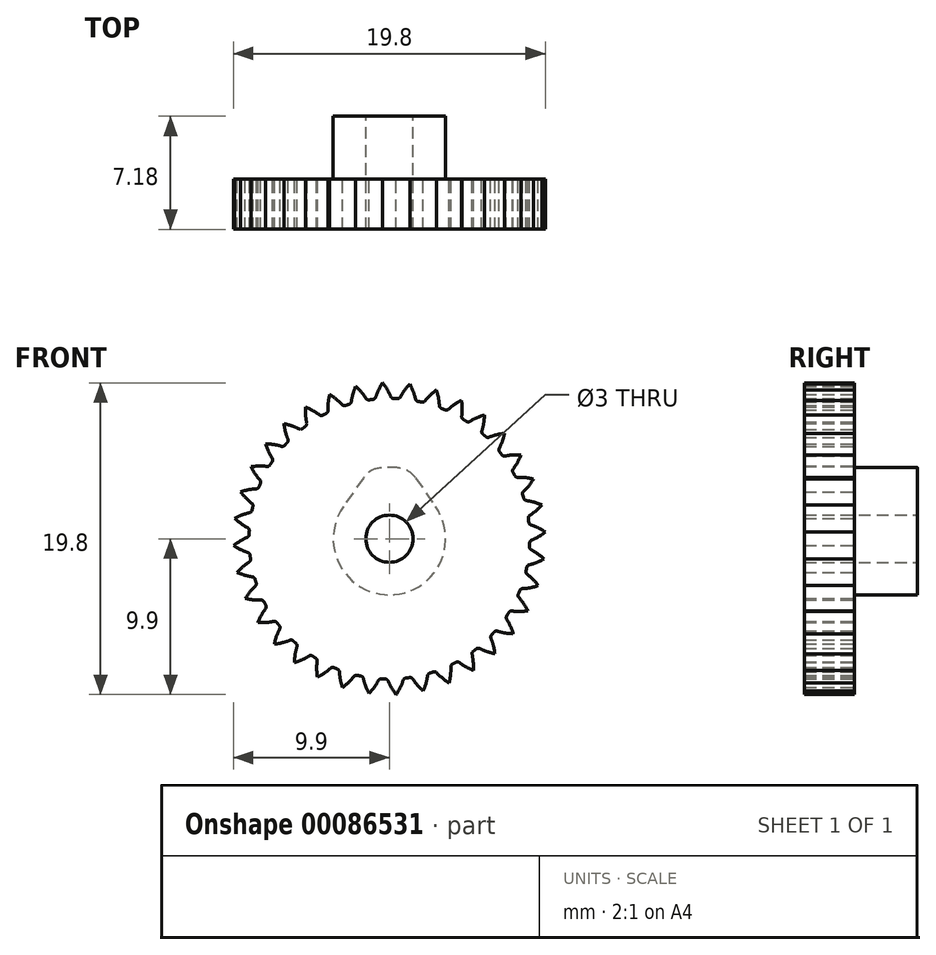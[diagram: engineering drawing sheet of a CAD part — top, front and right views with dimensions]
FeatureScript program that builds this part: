
annotation { "Feature Type Name" : "Feature", "Feature Type Description" : "" }
export const myFeature = defineFeature(function(context is Context, id is Id, definition is map)
    precondition{}
    {
        {
            assignVariable(context, id + "F0", {"name" : "Teeth", "anyValue" : 36});
        }
        {
            var Q0;
            Q0=qCreatedBy(makeId("Front.planeOp"),FACE);
            var sketch = newSketch(context, id + "F1", { "sketchPlane" : qUnion([Q0])});
            skCircle(sketch, "E0", {"center": v(0, 0) * mm, "radius": 8.49 * mm, "construction": true});
            skLineSegment(sketch, "E1", {"start": v(0, 0) * mm, "end": v(-0.32, 8.48) * mm, "construction": true});
            skLineSegment(sketch, "E2", {"start": v(0, 0) * mm, "end": v(-0.87, 8.44) * mm, "construction": true});
            skLineSegment(sketch, "E3", {"start": v(0, 0) * mm, "end": v(-1.41, 8.37) * mm, "construction": true});
            skLineSegment(sketch, "E4", {"start": v(-1.41, 8.37) * mm, "end": v(0.2, 8.64) * mm, "construction": true});
            skLineSegment(sketch, "E5", {"start": v(0, 0) * mm, "end": v(-1.95, 8.26) * mm, "construction": true});
            skLineSegment(sketch, "E6", {"start": v(-1.95, 8.26) * mm, "end": v(0.18, 8.76) * mm, "construction": true});
            skLineSegment(sketch, "E7", {"start": v(-1.41, 8.37) * mm, "end": v(-0.87, 8.44) * mm, "construction": true});
            skLineSegment(sketch, "E8", {"start": v(-1.95, 8.26) * mm, "end": v(-1.41, 8.37) * mm, "construction": true});
            skLineSegment(sketch, "E9", {"start": v(-1.41, 8.37) * mm, "end": v(-0.32, 8.48) * mm, "construction": true});
            skLineSegment(sketch, "E10", {"start": v(-1.95, 8.26) * mm, "end": v(-0.32, 8.48) * mm, "construction": true});
            skLineSegment(sketch, "E11", {"start": v(0, 0) * mm, "end": v(-3.5, 7.73) * mm, "construction": true});
            skLineSegment(sketch, "E12", {"start": v(-3.5, 7.73) * mm, "end": v(-0.04, 9.3) * mm, "construction": true});
            skLineSegment(sketch, "E13", {"start": v(0, 0) * mm, "end": v(-3, 7.94) * mm, "construction": true});
            skLineSegment(sketch, "E14", {"start": v(-3, 7.94) * mm, "end": v(0.06, 9.1) * mm, "construction": true});
            skLineSegment(sketch, "E15", {"start": v(0, 0) * mm, "end": v(-2.48, 8.12) * mm, "construction": true});
            skLineSegment(sketch, "E16", {"start": v(-2.48, 8.12) * mm, "end": v(0.13, 8.91) * mm, "construction": true});
            skLineSegment(sketch, "E17", {"start": v(-2.48, 8.12) * mm, "end": v(-1.95, 8.26) * mm, "construction": true});
            skLineSegment(sketch, "E18", {"start": v(-2.48, 8.12) * mm, "end": v(-3, 7.94) * mm, "construction": true});
            skLineSegment(sketch, "E19", {"start": v(-3, 7.94) * mm, "end": v(-3.5, 7.73) * mm, "construction": true});
            skLineSegment(sketch, "E20", {"start": v(-2.48, 8.12) * mm, "end": v(-0.32, 8.48) * mm, "construction": true});
            skLineSegment(sketch, "E21", {"start": v(-3, 7.94) * mm, "end": v(-0.32, 8.48) * mm, "construction": true});
            skLineSegment(sketch, "E22", {"start": v(-3.5, 7.73) * mm, "end": v(-0.32, 8.48) * mm, "construction": true});
            skLineSegment(sketch, "E23", {"start": v(0, 0) * mm, "end": v(-4.47, 7.21) * mm, "construction": true});
            skLineSegment(sketch, "E24", {"start": v(-4.47, 7.21) * mm, "end": v(-0.34, 9.78) * mm, "construction": true});
            skLineSegment(sketch, "E25", {"start": v(0, 0) * mm, "end": v(-4.93, 6.9) * mm, "construction": true});
            skLineSegment(sketch, "E26", {"start": v(-4.93, 6.9) * mm, "end": v(-0.54, 10.04) * mm, "construction": true});
            skLineSegment(sketch, "E27", {"start": v(0, 0) * mm, "end": v(-5.37, 6.58) * mm, "construction": true});
            skLineSegment(sketch, "E28", {"start": v(0, 0) * mm, "end": v(-4, 7.49) * mm, "construction": true});
            skLineSegment(sketch, "E29", {"start": v(-4, 7.49) * mm, "end": v(-0.17, 9.53) * mm, "construction": true});
            skLineSegment(sketch, "E30", {"start": v(-3.5, 7.73) * mm, "end": v(-4, 7.49) * mm, "construction": true});
            skLineSegment(sketch, "E31", {"start": v(-4, 7.49) * mm, "end": v(-4.47, 7.21) * mm, "construction": true});
            skLineSegment(sketch, "E32", {"start": v(-4.47, 7.21) * mm, "end": v(-4.93, 6.9) * mm, "construction": true});
            skLineSegment(sketch, "E33", {"start": v(-4.93, 6.9) * mm, "end": v(-5.37, 6.58) * mm, "construction": true});
            skLineSegment(sketch, "E34", {"start": v(-0.32, 8.48) * mm, "end": v(-4, 7.49) * mm, "construction": true});
            skLineSegment(sketch, "E35", {"start": v(-0.32, 8.48) * mm, "end": v(-4.47, 7.21) * mm, "construction": true});
            skLineSegment(sketch, "E36", {"start": v(-0.32, 8.48) * mm, "end": v(-4.93, 6.9) * mm, "construction": true});
            skLineSegment(sketch, "E37", {"start": v(-0.32, 8.48) * mm, "end": v(-5.37, 6.58) * mm, "construction": true});
            skCircle(sketch, "E38", {"center": v(0, 0) * mm, "radius": 9.53 * mm, "construction": true});
            skCircle(sketch, "E39", {"center": v(0, 0) * mm, "radius": 10.05 * mm});
            skPoint(sketch, "E40", {"position": v(0, 9.53) * mm});
            skLineSegment(sketch, "E41", {"start": v(0, 0) * mm, "end": v(-0.38, 8.6) * mm, "construction": true});
            skPoint(sketch, "E42.MirrorP", {"position": v(-0.83, 9.49) * mm});
            skLineSegment(sketch, "E43", {"start": v(-0.83, 9.49) * mm, "end": v(0, 0) * mm, "construction": true});
            skLineSegment(sketch, "E44", {"start": v(0, 0) * mm, "end": v(0, 9.53) * mm, "construction": true});
            skLineSegment(sketch, "E45", {"start": v(-0.87, 8.44) * mm, "end": v(-0.32, 8.48) * mm, "construction": true});
            skLineSegment(sketch, "E46", {"start": v(0.2, 8.64) * mm, "end": v(0.18, 8.76) * mm, "construction": true});
            skLineSegment(sketch, "E47", {"start": v(0, 0) * mm, "end": v(0, 10.19) * mm, "construction": true});
            skCircle(sketch, "E48", {"center": v(0, 0) * mm, "radius": 8.91 * mm});
            skSolve(sketch);
        }
        {
            var Q0;
            Q0=qCreatedBy(makeId("Front.planeOp"),FACE);
            var sketch = newSketch(context, id + "F2", { "sketchPlane" : qUnion([Q0])});
            skCircle(sketch, "E49.0", {"center": v(0, 0) * mm, "radius": 9.53 * mm, "construction": true});
            skPoint(sketch, "E50.0", {"position": v(-0.54, 10.04) * mm});
            skPoint(sketch, "E50.1", {"position": v(-0.34, 9.78) * mm});
            skPoint(sketch, "E50.2", {"position": v(-0.17, 9.53) * mm});
            skPoint(sketch, "E50.3", {"position": v(-0.04, 9.3) * mm});
            skPoint(sketch, "E50.4", {"position": v(0.06, 9.1) * mm});
            skPoint(sketch, "E50.6", {"position": v(0.18, 8.76) * mm});
            skPoint(sketch, "E50.7", {"position": v(0.2, 8.64) * mm});
            skPoint(sketch, "E50.8", {"position": v(0.13, 8.91) * mm});
            skLineSegment(sketch, "E51.0", {"start": v(0, 0) * mm, "end": v(-0.38, 8.6) * mm, "construction": true});
            skFitSpline(sketch, "E52", {"points": [v(-0.54, 10.04) * mm, v(-0.34, 9.78) * mm, v(-0.17, 9.53) * mm, v(-0.04, 9.3) * mm, v(0.06, 9.1) * mm, v(0.13, 8.91) * mm, v(0.18, 8.76) * mm, v(0.2, 8.64) * mm], "startDerivative": vector(3.53, -4.5) * mm, "endDerivative": vector(0.8, -3.4) * mm});
            skFitSpline(sketch, "E53.MirrorCS", {"points": [v(-0.34, 10.05) * mm, v(-0.52, 9.77) * mm, v(-0.66, 9.5) * mm, v(-0.77, 9.27) * mm, v(-0.85, 9.06) * mm, v(-0.9, 8.87) * mm, v(-0.94, 8.71) * mm, v(-0.96, 8.6) * mm], "startDerivative": vector(-3.13, -4.8) * mm, "endDerivative": vector(-0.5, -3.46) * mm});
            skCircle(sketch, "E54", {"center": v(0, 0) * mm, "radius": 1.5 * mm});
            skCircle(sketch, "E55.0", {"center": v(0, 0) * mm, "radius": 8.91 * mm});
            skArc(sketch, "E56", {"start": v(-0.54, 10.04) * mm, "mid": v(0.44, -10.04) * mm, "end": v(-0.34, 10.05) * mm});
            skLineSegment(sketch, "E57", {"start": v(-0.96, 8.6) * mm, "end": v(0, 0) * mm});
            skLineSegment(sketch, "E58", {"start": v(0, 0) * mm, "end": v(0.2, 8.64) * mm});
            skSolve(sketch);
        }
        {
            var Q0;
            {var subQ1=sQuery(id+"F2.wireOp",EDGE,"E52");var subQ9=sQuery(id+"F2.wireOp",EDGE,"rA0usyOi-Jm6w-jZNR-JSDv-ujEcH4bsm2Ol");var subQ11=makeQuery(id+"F2.imprint","INTERSECT",VERTEX,{"derivedFrom":[subQ1,subQ9]});Q0=makeQuery(id+"F2.imprint","IMPRINT",FACE,{"disambiguationData":[TD([[makeQuery(id+"F2.imprint","IMPRINT",EDGE,{"disambiguationData":[TD([[subQ11,1.0]])],"derivedFrom":subQ1}),-1.0]])]});}
            var Q1;
            {var subQ0=sQuery(id+"F2.wireOp",EDGE,"QqPcIgQ4-TZE6-73E5-WQaq-ugCT5JtziKyn");var subQ1=sQuery(id+"F2.wireOp",EDGE,"90be38e0-c88f-493d-85a8-1201295b9109.0");var subQ2=makeQuery(id+"F2.imprint","INTERSECT",VERTEX,{"derivedFrom":[subQ1,subQ0]});Q1=makeQuery(id+"F2.imprint","IMPRINT",FACE,{"disambiguationData":[TD([[makeQuery(id+"F2.imprint","IMPRINT",EDGE,{"disambiguationData":[TD([[subQ2,1.0]])],"derivedFrom":subQ1}),1.0]])]});}
            var Q2;
            {var subQ0=sQuery(id+"F2.wireOp",EDGE,"QqPcIgQ4-TZE6-73E5-WQaq-ugCT5JtziKyn");var subQ1=sQuery(id+"F2.wireOp",EDGE,"90be38e0-c88f-493d-85a8-1201295b9109.0");var subQ2=makeQuery(id+"F2.imprint","INTERSECT",VERTEX,{"derivedFrom":[subQ1,subQ0]});Q2=makeQuery(id+"F2.imprint","IMPRINT",FACE,{"disambiguationData":[TD([[makeQuery(id+"F2.imprint","IMPRINT",EDGE,{"disambiguationData":[TD([[subQ2,-1.0]])],"derivedFrom":subQ1}),1.0]])]});}
            var Q3;
            {var subQ1=sQuery(id+"F2.wireOp",EDGE,"E52");var subQ8=sQuery(id+"F2.wireOp",EDGE,"b861a5ab-cd51-40f1-92ab-cea0f5fe0d4d.1");var subQ11=makeQuery(id+"F2.imprint","INTERSECT",VERTEX,{"derivedFrom":[subQ1,subQ8]});Q3=makeQuery(id+"F2.imprint","IMPRINT",FACE,{"disambiguationData":[TD([[makeQuery(id+"F2.imprint","IMPRINT",EDGE,{"disambiguationData":[TD([[subQ11,1.0]])],"derivedFrom":subQ1}),-1.0]])]});}
            var Q4;
            {var subQ0=sQuery(id+"F2.wireOp",EDGE,"b861a5ab-cd51-40f1-92ab-cea0f5fe0d4d.0");var subQ1=sQuery(id+"F2.wireOp",EDGE,"E54");var subQ2=makeQuery(id+"F2.imprint","INTERSECT",VERTEX,{"derivedFrom":[subQ1,subQ0]});Q4=makeQuery(id+"F2.imprint","IMPRINT",FACE,{"disambiguationData":[TD([[makeQuery(id+"F2.imprint","IMPRINT",EDGE,{"disambiguationData":[TD([[subQ2,-1.0]])],"derivedFrom":subQ1}),-1.0]])]});}
            var Q5;
            {var subQ0=sQuery(id+"F2.wireOp",EDGE,"b861a5ab-cd51-40f1-92ab-cea0f5fe0d4d.0");var subQ1=sQuery(id+"F2.wireOp",EDGE,"E54");var subQ2=makeQuery(id+"F2.imprint","INTERSECT",VERTEX,{"derivedFrom":[subQ1,subQ0]});Q5=makeQuery(id+"F2.imprint","IMPRINT",FACE,{"disambiguationData":[TD([[makeQuery(id+"F2.imprint","IMPRINT",EDGE,{"disambiguationData":[TD([[subQ2,1.0]])],"derivedFrom":subQ1}),-1.0]])]});}
            extrude(context, id + "F3", {"entities" : qUnion([Q0, Q1, Q2, Q3, Q4, Q5]), "depth" : 3.17 * mm});
        }
        {
            var Q0;
            Q0=makeQuery(id+"F3.opExtrude","SWEPT_EDGE",EDGE,{"disambiguationData":[OSD([sQuery(id+"F2.wireOp",EDGE,"b861a5ab-cd51-40f1-92ab-cea0f5fe0d4d.1"),sQuery(id+"F2.wireOp",EDGE,"E55.0")])]});
            var Q1;
            Q1=makeQuery(id+"F3.opExtrude","SWEPT_EDGE",EDGE,{"disambiguationData":[OSD([sQuery(id+"F2.wireOp",EDGE,"b861a5ab-cd51-40f1-92ab-cea0f5fe0d4d.0"),sQuery(id+"F2.wireOp",EDGE,"E55.0")])]});
            fillet(context, id + "F4", {"entities" : qUnion([Q0, Q1]), "radius" : 0.2 * mm, "tangentPropagation" : true, "allowEdgeOverflow" : false});
        }
        {
            var Q0;
            Q0=makeQuery(id+"F4.opFillet","BLEND_FACE",FACE,{"disambiguationData":[OSD([sQuery(id+"F2.wireOp",EDGE,"E55.0"),sQuery(id+"F2.wireOp",EDGE,"E57")])]});
            var Q1;
            Q1=makeQuery(id+"F3.opExtrude","SWEPT_FACE",FACE,{"disambiguationData":[OSD([sQuery(id+"F2.wireOp",EDGE,"E57")])]});
            var Q2;
            Q2=makeQuery(id+"F3.opExtrude","SWEPT_FACE",FACE,{"disambiguationData":[OSD([sQuery(id+"F2.wireOp",EDGE,"E53.MirrorCS")])]});
            var Q3;
            Q3=makeQuery(id+"F3.opExtrude","SWEPT_FACE",FACE,{"disambiguationData":[OSD([sQuery(id+"F2.wireOp",EDGE,"E56")])]});
            var Q4;
            Q4=makeQuery(id+"F3.opExtrude","SWEPT_FACE",FACE,{"disambiguationData":[OSD([sQuery(id+"F2.wireOp",EDGE,"E52")])]});
            var Q5;
            Q5=makeQuery(id+"F3.opExtrude","SWEPT_FACE",FACE,{"disambiguationData":[OSD([sQuery(id+"F2.wireOp",EDGE,"E58")])]});
            var Q6;
            Q6=makeQuery(id+"F4.opFillet","BLEND_FACE",FACE,{"disambiguationData":[OSD([sQuery(id+"F2.wireOp",EDGE,"E55.0"),sQuery(id+"F2.wireOp",EDGE,"E58")])]});
            var Q7;
            Q7=makeQuery(id+"F3.opExtrude","SWEPT_FACE",FACE,{"disambiguationData":[OSD([sQuery(id+"F2.wireOp",EDGE,"E55.0")])]});
            circularPattern(context, id + "F5", {"faces" : qUnion([Q0, Q1, Q2, Q3, Q4, Q5, Q6]), "axis" : qUnion([Q7]), "angle" : 360 * degree, "instanceCount" : round(getVariable(context, 'Teeth')), "equalSpace" : true, "patternType" : PatternType.FACE});
        }
        {
            var Q0;
            Q0=makeQuery(id+"F3.opExtrude","CAP_FACE",FACE,{"disambiguationData":[OSD([sQuery(id+"F2.wireOp",EDGE,"E52"),sQuery(id+"F2.wireOp",EDGE,"E53.MirrorCS"),sQuery(id+"F2.wireOp",EDGE,"E54"),sQuery(id+"F2.wireOp",EDGE,"E55.0")])],"isStart":true});
            var sketch = newSketch(context, id + "F6", { "sketchPlane" : qUnion([Q0])});
            skCircle(sketch, "E59", {"center": v(0, 0) * mm, "radius": 3.57 * mm});
            skArc(sketch, "E60", {"start": v(1.33, 4.34) * mm, "mid": v(0, 4.54) * mm, "end": v(-1.33, 4.34) * mm});
            skLineSegment(sketch, "E61", {"start": v(0, 0) * mm, "end": v(0, 6.8) * mm, "construction": true});
            skLineSegment(sketch, "E62", {"start": v(0, 4.54) * mm, "end": v(-1.33, 4.54) * mm, "construction": true});
            skLineSegment(sketch, "E63", {"start": v(0, 4.54) * mm, "end": v(1.33, 4.54) * mm, "construction": true});
            skLineSegment(sketch, "E64", {"start": v(-1.33, 4.54) * mm, "end": v(-1.33, 0) * mm, "construction": true});
            skLineSegment(sketch, "E65", {"start": v(1.33, 4.54) * mm, "end": v(1.33, 0) * mm, "construction": true});
            skPoint(sketch, "E66", {"position": v(-1.33, 4.34) * mm});
            skPoint(sketch, "E67", {"position": v(1.33, 4.34) * mm});
            skLineSegment(sketch, "E68", {"start": v(-1.33, 4.34) * mm, "end": v(-2.93, 2.04) * mm});
            skLineSegment(sketch, "E69", {"start": v(1.33, 4.34) * mm, "end": v(2.93, 2.04) * mm});
            skSolve(sketch);
        }
        {
            var Q0;
            Q0=makeQuery(id+"F6.imprint","IMPRINT",FACE,{"disambiguationData":[TD([[makeQuery(id+"F6.imprint","IMPRINT",EDGE,{"derivedFrom":makeQuery(id+"F3.opExtrude","CAP_EDGE",EDGE,{"disambiguationData":[OSD([sQuery(id+"F2.wireOp",EDGE,"E54")])],"isStart":true})}),1.0]])]});
            var Q1;
            Q1=makeQuery(id+"F6.imprint","IMPRINT",FACE,{"disambiguationData":[TD([[makeQuery(id+"F6.imprint","IMPRINT",EDGE,{"derivedFrom":sQuery(id+"F6.wireOp",EDGE,"E60")}),1.0]])]});
            extrude(context, id + "F7", {"entities" : qUnion([Q0, Q1]), "operationType" : NewBodyOperationType.ADD, "depth" : 4 * mm});
        }
        {
            var Q0;
            Q0=makeQuery(id+"F6.imprint","IMPRINT",FACE,{"disambiguationData":[TD([[makeQuery(id+"F6.imprint","IMPRINT",EDGE,{"derivedFrom":makeQuery(id+"F3.opExtrude","CAP_EDGE",EDGE,{"disambiguationData":[OSD([sQuery(id+"F2.wireOp",EDGE,"E54")])],"isStart":true})}),-1.0]])]});
            extrude(context, id + "F8", {"entities" : qUnion([Q0]), "operationType" : NewBodyOperationType.REMOVE, "depth" : 25 * mm, "symmetric" : true});
        }
        {
            var Q0;
            Q0=makeQuery(id+"F7.opExtrude","SWEPT_EDGE",EDGE,{"disambiguationData":[OSD([sQuery(id+"F6.wireOp",EDGE,"E60"),sQuery(id+"F6.wireOp",EDGE,"E69")])]});
            var Q1;
            Q1=makeQuery(id+"F7.opExtrude","SWEPT_EDGE",EDGE,{"disambiguationData":[OSD([sQuery(id+"F6.wireOp",EDGE,"E60"),sQuery(id+"F6.wireOp",EDGE,"E68")])]});
            fillet(context, id + "F9", {"entities" : qUnion([Q0, Q1]), "radius" : 1.5 * mm, "tangentPropagation" : true, "allowEdgeOverflow" : false});
        }
    });
